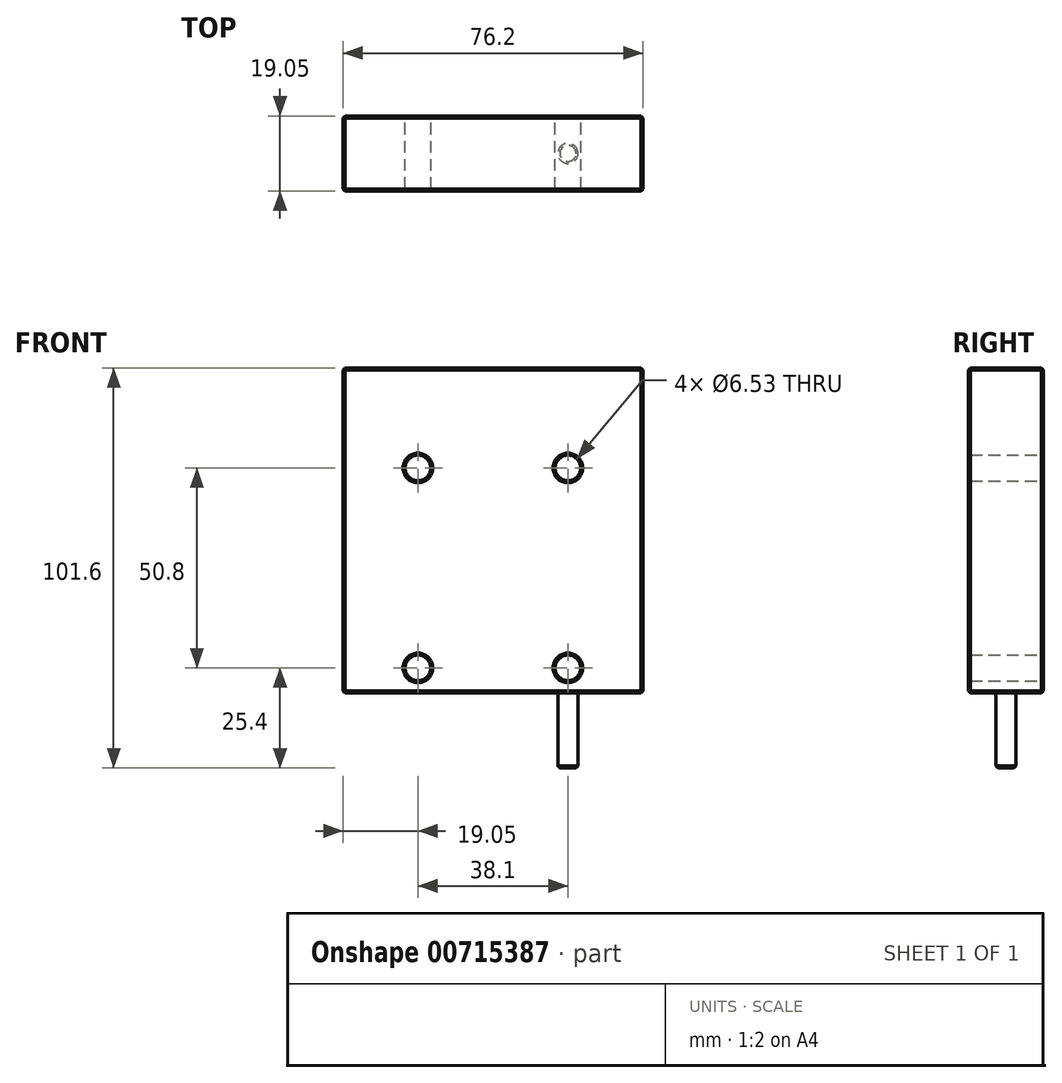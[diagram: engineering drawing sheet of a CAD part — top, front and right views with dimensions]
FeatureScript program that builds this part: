
annotation { "Feature Type Name" : "Feature", "Feature Type Description" : "" }
export const myFeature = defineFeature(function(context is Context, id is Id, definition is map)
    precondition{}
    {
        {
            var Q0;
            Q0=qCreatedBy(makeId("Front.planeOp"),FACE);
            var sketch = newSketch(context, id + "F0", { "sketchPlane" : qUnion([Q0])});
            skLineSegment(sketch, "E0.bottom", {"start": v(38.1, 50.8) * mm, "end": v(-38.1, 50.8) * mm});
            skLineSegment(sketch, "E0.top", {"start": v(38.1, -50.8) * mm, "end": v(-38.1, -50.8) * mm});
            skLineSegment(sketch, "E0.left", {"start": v(38.1, 50.8) * mm, "end": v(38.1, -50.8) * mm});
            skLineSegment(sketch, "E0.right", {"start": v(-38.1, 50.8) * mm, "end": v(-38.1, -50.8) * mm});
            skPoint(sketch, "E0.middle", {"position": v(0, 0) * mm});
            skLineSegment(sketch, "E1", {"start": v(-19.05, 50.8) * mm, "end": v(-19.05, -50.8) * mm, "construction": true});
            skLineSegment(sketch, "E2.MirrorCS", {"start": v(19.05, 50.8) * mm, "end": v(19.05, -50.8) * mm, "construction": true});
            skLineSegment(sketch, "E3", {"start": v(-38.1, 25.4) * mm, "end": v(38.1, 25.4) * mm, "construction": true});
            skCircle(sketch, "E4", {"center": v(-19.05, 25.4) * mm, "radius": 3.26 * mm});
            skCircle(sketch, "E5.MirrorC", {"center": v(19.05, 25.4) * mm, "radius": 3.26 * mm});
            skCircle(sketch, "E6.MirrorC", {"center": v(-19.05, -25.4) * mm, "radius": 3.26 * mm});
            skCircle(sketch, "E7.MirrorC", {"center": v(19.05, -25.4) * mm, "radius": 3.26 * mm});
            skSolve(sketch);
        }
        {
            var Q0;
            Q0=makeQuery(id+"F0.imprint","IMPRINT",FACE,{"disambiguationData":[TD([[makeQuery(id+"F0.imprint","IMPRINT",EDGE,{"derivedFrom":sQuery(id+"F0.wireOp",EDGE,"E0.bottom")}),1.0]])]});
            extrude(context, id + "F1", {"entities" : qUnion([Q0]), "depth" : 19.05 * mm, "offsetDistance" : 25.4 * mm});
        }
        {
            var Q0;
            Q0=makeQuery(id+"F1.opExtrude","SWEPT_FACE",FACE,{"disambiguationData":[OSD([sQuery(id+"F0.wireOp",EDGE,"E0.top")])]});
            var sketch = newSketch(context, id + "F2", { "sketchPlane" : qUnion([Q0])});
            skLineSegment(sketch, "E8", {"start": v(-19.05, 19.05) * mm, "end": v(-19.05, 0) * mm, "construction": true});
            skLineSegment(sketch, "E9.MirrorCS", {"start": v(19.05, 19.05) * mm, "end": v(19.05, 0) * mm, "construction": true});
            skCircle(sketch, "E10", {"center": v(-19.05, 9.53) * mm, "radius": 2.55 * mm});
            skCircle(sketch, "E11.MirrorC", {"center": v(19.05, 9.53) * mm, "radius": 2.55 * mm});
            skSolve(sketch);
        }
        {
            var Q0;
            Q0=makeQuery(id+"F2.imprint","IMPRINT",FACE,{"disambiguationData":[TD([[makeQuery(id+"F2.imprint","IMPRINT",EDGE,{"derivedFrom":sQuery(id+"F2.wireOp",EDGE,"E10")}),1.0]])]});
            var Q1;
            Q1=makeQuery(id+"F2.imprint","IMPRINT",FACE,{"disambiguationData":[TD([[makeQuery(id+"F2.imprint","IMPRINT",EDGE,{"derivedFrom":sQuery(id+"F2.wireOp",EDGE,"E11.MirrorC")}),-1.0]])]});
            extrude(context, id + "F3", {"entities" : qUnion([Q0, Q1]), "operationType" : NewBodyOperationType.REMOVE, "oppositeDirection" : true, "depth" : 19.05 * mm, "offsetDistance" : 25.4 * mm});
        }
        {
            var Q0;
            Q0=makeQuery(id+"F1.opExtrude","CAP_FACE",FACE,{"disambiguationData":[OSD([sQuery(id+"F0.wireOp",EDGE,"E0.bottom"),sQuery(id+"F0.wireOp",EDGE,"E0.top"),sQuery(id+"F0.wireOp",EDGE,"E0.left"),sQuery(id+"F0.wireOp",EDGE,"E0.right"),sQuery(id+"F0.wireOp",EDGE,"E4"),sQuery(id+"F0.wireOp",EDGE,"E5.MirrorC"),sQuery(id+"F0.wireOp",EDGE,"E6.MirrorC"),sQuery(id+"F0.wireOp",EDGE,"E7.MirrorC")])],"isStart":false});
            var Q1;
            Q1=makeQuery(id+"F1.opExtrude","SWEPT_FACE",FACE,{"disambiguationData":[OSD([sQuery(id+"F0.wireOp",EDGE,"E0.right")])]});
            var Q2;
            Q2=makeQuery(id+"F1.opExtrude","SWEPT_FACE",FACE,{"disambiguationData":[OSD([sQuery(id+"F0.wireOp",EDGE,"E0.top")])]});
            var Q3;
            Q3=makeQuery(id+"F1.opExtrude","CAP_FACE",FACE,{"disambiguationData":[OSD([sQuery(id+"F0.wireOp",EDGE,"E0.bottom"),sQuery(id+"F0.wireOp",EDGE,"E0.top"),sQuery(id+"F0.wireOp",EDGE,"E0.left"),sQuery(id+"F0.wireOp",EDGE,"E0.right"),sQuery(id+"F0.wireOp",EDGE,"E4"),sQuery(id+"F0.wireOp",EDGE,"E5.MirrorC"),sQuery(id+"F0.wireOp",EDGE,"E6.MirrorC"),sQuery(id+"F0.wireOp",EDGE,"E7.MirrorC")])],"isStart":true});
            var Q4;
            Q4=makeQuery(id+"F1.opExtrude","SWEPT_FACE",FACE,{"disambiguationData":[OSD([sQuery(id+"F0.wireOp",EDGE,"E0.left")])]});
            var Q5;
            Q5=makeQuery(id+"F1.opExtrude","SWEPT_FACE",FACE,{"disambiguationData":[OSD([sQuery(id+"F0.wireOp",EDGE,"E0.bottom")])]});
            chamfer(context, id + "F4", {"entities" : qUnion([Q0, Q1, Q2, Q3, Q4, Q5]), "width" : 0.5 * mm, "tangentPropagation" : true});
        }
    });
